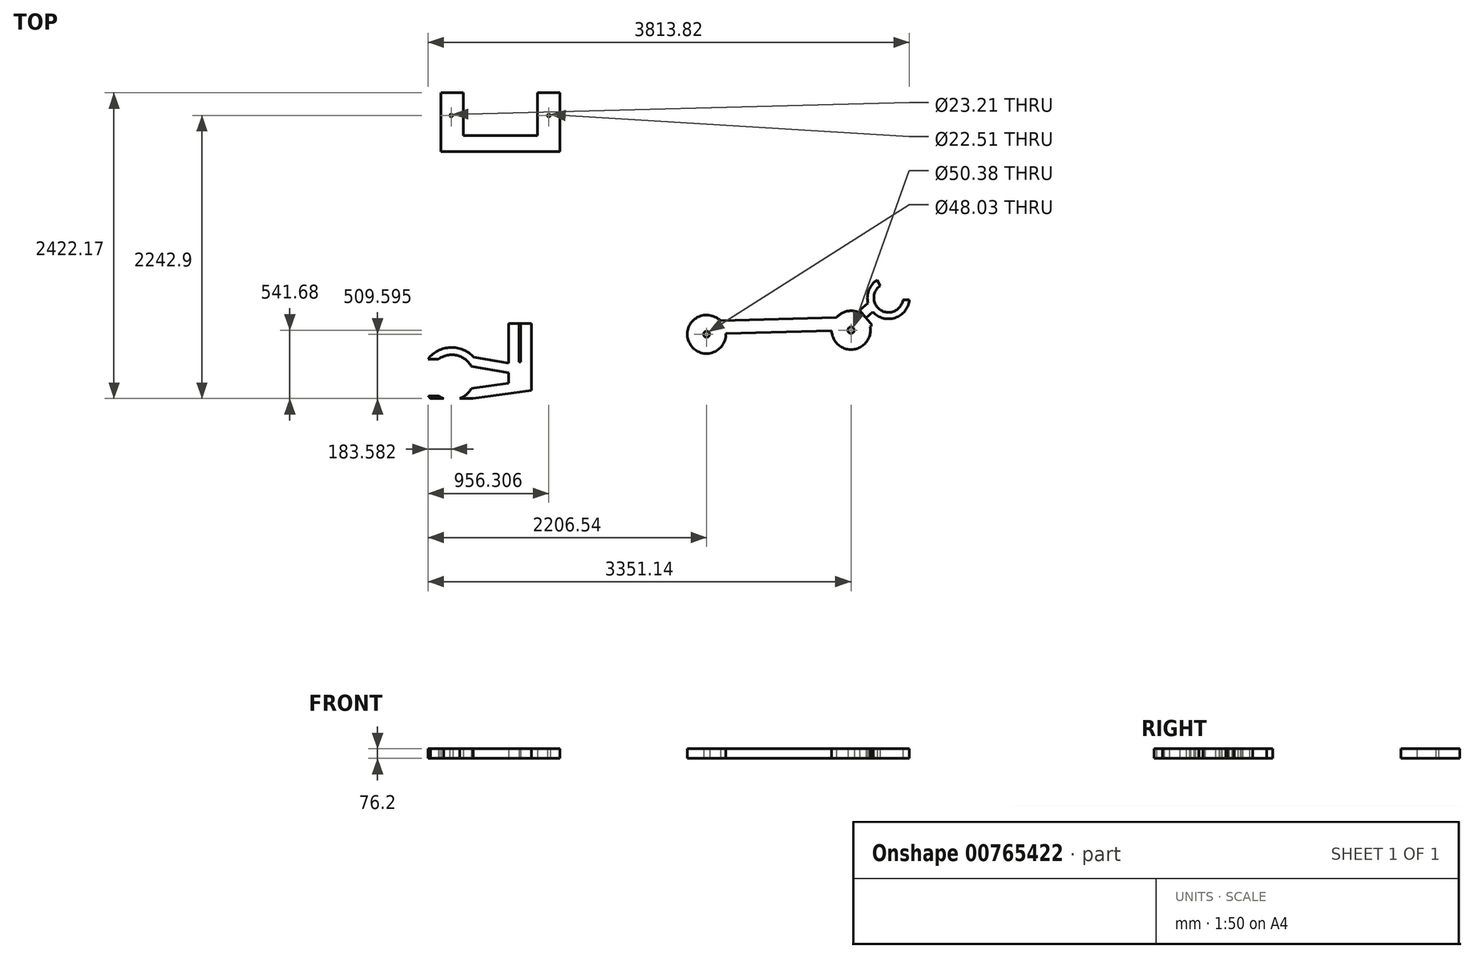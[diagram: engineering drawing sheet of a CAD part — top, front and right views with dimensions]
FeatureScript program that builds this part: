
annotation { "Feature Type Name" : "Feature", "Feature Type Description" : "" }
export const myFeature = defineFeature(function(context is Context, id is Id, definition is map)
    precondition{}
    {
        {
            var Q0;
            Q0=qCreatedBy(makeId("Top.planeOp"),FACE);
            var sketch = newSketch(context, id + "F0", { "sketchPlane" : qUnion([Q0])});
            skCircle(sketch, "E0", {"center": v(-167.25, 5.31) * mm, "radius": 152.85 * mm});
            skLineSegment(sketch, "E1", {"start": v(-167.25, 5.31) * mm, "end": v(977.35, 37.4) * mm});
            skCircle(sketch, "E2", {"center": v(977.35, 37.4) * mm, "radius": 153.41 * mm});
            skLineSegment(sketch, "E3", {"start": v(405.05, 21.36) * mm, "end": v(407.92, -80.8) * mm});
            skLineSegment(sketch, "E4", {"start": v(407.92, -80.8) * mm, "end": v(405.05, 21.36) * mm});
            skLineSegment(sketch, "E5", {"start": v(405.05, 21.36) * mm, "end": v(402.17, 124.37) * mm});
            skLineSegment(sketch, "E6", {"start": v(402.17, 124.37) * mm, "end": v(960.37, 140.02) * mm});
            skLineSegment(sketch, "E7", {"start": v(402.17, 124.37) * mm, "end": v(-140.1, 109.17) * mm});
            skLineSegment(sketch, "E8", {"start": v(407.92, -80.8) * mm, "end": v(-155.3, -80.8) * mm});
            skLineSegment(sketch, "E9", {"start": v(407.92, -80.8) * mm, "end": v(986.6, -64.59) * mm});
            skLineSegment(sketch, "E10", {"start": v(986.6, -64.59) * mm, "end": v(960.37, 122.33) * mm});
            skLineSegment(sketch, "E11", {"start": v(-155.3, -80.8) * mm, "end": v(-140.1, 109.17) * mm});
            skLineSegment(sketch, "E12", {"start": v(960.37, 122.33) * mm, "end": v(960.37, 140.02) * mm});
            skLineSegment(sketch, "E13", {"start": v(977.35, 37.4) * mm, "end": v(1190.16, 214.86) * mm});
            skLineSegment(sketch, "E14", {"start": v(1095.18, 135.65) * mm, "end": v(1044.8, 196.07) * mm});
            skLineSegment(sketch, "E15", {"start": v(1044.8, 196.07) * mm, "end": v(1144.24, 76.82) * mm});
            skLineSegment(sketch, "E16", {"start": v(1144.24, 76.82) * mm, "end": v(1240.32, 156.95) * mm});
            skLineSegment(sketch, "E17", {"start": v(1240.32, 156.95) * mm, "end": v(1095.18, 35.9) * mm});
            skLineSegment(sketch, "E18", {"start": v(1095.18, 35.9) * mm, "end": v(998.06, 152.36) * mm});
            skLineSegment(sketch, "E19", {"start": v(1044.8, 196.07) * mm, "end": v(995.52, 154.98) * mm});
            skLineSegment(sketch, "E20", {"start": v(995.52, 154.98) * mm, "end": v(1139.78, 275.28) * mm});
            skCircle(sketch, "E21", {"center": v(1273.88, 293.87) * mm, "radius": 115.64 * mm});
            skCircle(sketch, "E22", {"center": v(1273.88, 293.87) * mm, "radius": 166.9 * mm});
            skLineSegment(sketch, "E23", {"start": v(1185.71, 435.58) * mm, "end": v(1207.84, 388.8) * mm});
            skLineSegment(sketch, "E24", {"start": v(1388.44, 278.11) * mm, "end": v(1440.03, 278.11) * mm});
            skCircle(sketch, "E25", {"center": v(-167.25, 5.31) * mm, "radius": 24.02 * mm});
            skCircle(sketch, "E26", {"center": v(977.35, 37.4) * mm, "radius": 25.2 * mm});
            skSolve(sketch);
        }
        {
            var Q0;
            {var subQ0=sQuery(id+"F0.wireOp",EDGE,"E17");var subQ3=sQuery(id+"F0.wireOp",EDGE,"E15");var subQ5=makeQuery(id+"F0.imprint","INTERSECT",VERTEX,{"derivedFrom":[subQ3,subQ0]});Q0=makeQuery(id+"F0.imprint","IMPRINT",FACE,{"disambiguationData":[TD([[makeQuery(id+"F0.imprint","IMPRINT",EDGE,{"disambiguationData":[TD([[subQ5,-1.0]])],"derivedFrom":subQ0}),-1.0]])]});}
            var Q1;
            {var subQ0=sQuery(id+"F0.wireOp",EDGE,"E20");var subQ3=sQuery(id+"F0.wireOp",EDGE,"E15");var subQ5=makeQuery(id+"F0.imprint","INTERSECT",VERTEX,{"derivedFrom":[subQ3,subQ0]});Q1=makeQuery(id+"F0.imprint","IMPRINT",FACE,{"disambiguationData":[TD([[makeQuery(id+"F0.imprint","IMPRINT",EDGE,{"disambiguationData":[TD([[subQ5,1.0]])],"derivedFrom":subQ0}),-1.0]])]});}
            var Q2;
            {var subQ5=sQuery(id+"F0.wireOp",EDGE,"E5");Q2=makeQuery(id+"F0.imprint","IMPRINT",FACE,{"disambiguationData":[TD([[makeQuery(id+"F0.imprint","IMPRINT",EDGE,{"derivedFrom":subQ5}),1.0]])]});}
            var Q3;
            {var subQ5=sQuery(id+"F0.wireOp",EDGE,"E0");var subQ7=sQuery(id+"F0.wireOp",EDGE,"E7");var subQ8=makeQuery(id+"F0.imprint","INTERSECT",VERTEX,{"derivedFrom":[subQ5,subQ7]});Q3=makeQuery(id+"F0.imprint","IMPRINT",FACE,{"disambiguationData":[TD([[makeQuery(id+"F0.imprint","IMPRINT",EDGE,{"disambiguationData":[TD([[subQ8,-1.0]])],"derivedFrom":subQ5}),1.0]])]});}
            var Q4;
            {var subQ5=sQuery(id+"F0.wireOp",EDGE,"E4");Q4=makeQuery(id+"F0.imprint","IMPRINT",FACE,{"disambiguationData":[TD([[makeQuery(id+"F0.imprint","IMPRINT",EDGE,{"derivedFrom":subQ5}),1.0]])]});}
            var Q5;
            {var subQ0=sQuery(id+"F0.wireOp",EDGE,"E5");Q5=makeQuery(id+"F0.imprint","IMPRINT",FACE,{"disambiguationData":[TD([[makeQuery(id+"F0.imprint","IMPRINT",EDGE,{"derivedFrom":subQ0}),-1.0]])]});}
            var Q6;
            {var subQ0=sQuery(id+"F0.wireOp",EDGE,"E4");Q6=makeQuery(id+"F0.imprint","IMPRINT",FACE,{"disambiguationData":[TD([[makeQuery(id+"F0.imprint","IMPRINT",EDGE,{"derivedFrom":subQ0}),-1.0]])]});}
            var Q7;
            {var subQ0=sQuery(id+"F0.wireOp",EDGE,"E17");var subQ5=sQuery(id+"F0.wireOp",EDGE,"E18");var subQ6=makeQuery(id+"F0.imprint","INTERSECT",VERTEX,{"derivedFrom":[subQ0,subQ5]});Q7=makeQuery(id+"F0.imprint","IMPRINT",FACE,{"disambiguationData":[TD([[makeQuery(id+"F0.imprint","IMPRINT",EDGE,{"disambiguationData":[TD([[subQ6,1.0]])],"derivedFrom":subQ0}),-1.0]])]});}
            var Q8;
            {var subQ3=sQuery(id+"F0.wireOp",EDGE,"E15");var subQ5=sQuery(id+"F0.wireOp",EDGE,"E20");var subQ6=makeQuery(id+"F0.imprint","INTERSECT",VERTEX,{"derivedFrom":[subQ3,subQ5]});Q8=makeQuery(id+"F0.imprint","IMPRINT",FACE,{"disambiguationData":[TD([[makeQuery(id+"F0.imprint","IMPRINT",EDGE,{"disambiguationData":[TD([[subQ6,-1.0]])],"derivedFrom":subQ5}),-1.0]])]});}
            var Q9;
            {var subQ3=sQuery(id+"F0.wireOp",EDGE,"E15");var subQ5=sQuery(id+"F0.wireOp",EDGE,"E17");var subQ7=makeQuery(id+"F0.imprint","INTERSECT",VERTEX,{"derivedFrom":[subQ3,subQ5]});Q9=makeQuery(id+"F0.imprint","IMPRINT",FACE,{"disambiguationData":[TD([[makeQuery(id+"F0.imprint","IMPRINT",EDGE,{"disambiguationData":[TD([[subQ7,1.0]])],"derivedFrom":subQ5}),-1.0]])]});}
            var Q10;
            {var subQ1=sQuery(id+"F0.wireOp",EDGE,"E7");var subQ5=sQuery(id+"F0.wireOp",EDGE,"E0");var subQ6=makeQuery(id+"F0.imprint","INTERSECT",VERTEX,{"derivedFrom":[subQ5,subQ1]});Q10=makeQuery(id+"F0.imprint","IMPRINT",FACE,{"disambiguationData":[TD([[makeQuery(id+"F0.imprint","IMPRINT",EDGE,{"disambiguationData":[TD([[subQ6,1.0]])],"derivedFrom":subQ5}),1.0]])]});}
            var Q11;
            {var subQ1=sQuery(id+"F0.wireOp",EDGE,"E8");var subQ5=sQuery(id+"F0.wireOp",EDGE,"E0");var subQ6=makeQuery(id+"F0.imprint","INTERSECT",VERTEX,{"derivedFrom":[subQ5,subQ1]});Q11=makeQuery(id+"F0.imprint","IMPRINT",FACE,{"disambiguationData":[TD([[makeQuery(id+"F0.imprint","IMPRINT",EDGE,{"disambiguationData":[TD([[subQ6,-1.0]])],"derivedFrom":subQ5}),1.0]])]});}
            var Q12;
            {var subQ0=sQuery(id+"F0.wireOp",EDGE,"E12");Q12=makeQuery(id+"F0.imprint","IMPRINT",FACE,{"disambiguationData":[TD([[makeQuery(id+"F0.imprint","IMPRINT",EDGE,{"derivedFrom":subQ0}),1.0]])]});}
            var Q13;
            {var subQ5=sQuery(id+"F0.wireOp",EDGE,"E2");var subQ7=sQuery(id+"F0.wireOp",EDGE,"E1");var subQ8=makeQuery(id+"F0.imprint","INTERSECT",VERTEX,{"derivedFrom":[subQ7,subQ5]});Q13=makeQuery(id+"F0.imprint","IMPRINT",FACE,{"disambiguationData":[TD([[makeQuery(id+"F0.imprint","IMPRINT",EDGE,{"disambiguationData":[TD([[subQ8,-1.0]])],"derivedFrom":subQ7}),-1.0]])]});}
            var Q14;
            {var subQ8=sQuery(id+"F0.wireOp",EDGE,"E2");var subQ11=sQuery(id+"F0.wireOp",EDGE,"E17");var subQ12=makeQuery(id+"F0.imprint","INTERSECT",VERTEX,{"derivedFrom":[subQ8,subQ11]});Q14=makeQuery(id+"F0.imprint","IMPRINT",FACE,{"disambiguationData":[TD([[makeQuery(id+"F0.imprint","IMPRINT",EDGE,{"disambiguationData":[TD([[subQ12,1.0]])],"derivedFrom":subQ8}),1.0]])]});}
            var Q15;
            {var subQ4=sQuery(id+"F0.wireOp",EDGE,"E23");Q15=makeQuery(id+"F0.imprint","IMPRINT",FACE,{"disambiguationData":[TD([[makeQuery(id+"F0.imprint","IMPRINT",EDGE,{"derivedFrom":subQ4}),-1.0]])]});}
            var Q16;
            {var subQ4=sQuery(id+"F0.wireOp",EDGE,"E24");Q16=makeQuery(id+"F0.imprint","IMPRINT",FACE,{"disambiguationData":[TD([[makeQuery(id+"F0.imprint","IMPRINT",EDGE,{"derivedFrom":subQ4}),-1.0]])]});}
            var Q17;
            {var subQ0=sQuery(id+"F0.wireOp",EDGE,"E12");Q17=makeQuery(id+"F0.imprint","IMPRINT",FACE,{"disambiguationData":[TD([[makeQuery(id+"F0.imprint","IMPRINT",EDGE,{"derivedFrom":subQ0}),-1.0]])]});}
            extrude(context, id + "F1", {"entities" : qUnion([Q0, Q1, Q2, Q3, Q4, Q5, Q6, Q7, Q8, Q9, Q10, Q11, Q12, Q13, Q14, Q15, Q16, Q17]), "depth" : 76.2 * mm, "offsetDistance" : 25.4 * mm});
        }
        {
            var Q0;
            Q0=qCreatedBy(makeId("Top.planeOp"),FACE);
            var sketch = newSketch(context, id + "F2", { "sketchPlane" : qUnion([Q0])});
            skLineSegment(sketch, "E27.bottom", {"start": v(-1735.68, 90.3) * mm, "end": v(-1556.35, 90.3) * mm});
            skLineSegment(sketch, "E27.top", {"start": v(-1735.68, -438.7) * mm, "end": v(-1556.35, -438.7) * mm});
            skLineSegment(sketch, "E27.left", {"start": v(-1735.68, 90.3) * mm, "end": v(-1735.68, -438.7) * mm});
            skLineSegment(sketch, "E27.right", {"start": v(-1556.35, 90.3) * mm, "end": v(-1556.35, -438.7) * mm});
            skLineSegment(sketch, "E28", {"start": v(-1735.68, 90.3) * mm, "end": v(-1646.02, 90.3) * mm});
            skLineSegment(sketch, "E29", {"start": v(-1646.02, 90.3) * mm, "end": v(-1556.35, 90.3) * mm});
            skLineSegment(sketch, "E30", {"start": v(-1652.05, 90.42) * mm, "end": v(-1639.27, 90.3) * mm});
            skLineSegment(sketch, "E31", {"start": v(-1639.27, 90.3) * mm, "end": v(-1642.15, -215.01) * mm});
            skLineSegment(sketch, "E32", {"start": v(-1652.05, 90.42) * mm, "end": v(-1654.93, -214.97) * mm});
            skLineSegment(sketch, "E33", {"start": v(-1654.93, -214.97) * mm, "end": v(-1642.15, -215.01) * mm});
            skLineSegment(sketch, "E34", {"start": v(-1556.35, -438.7) * mm, "end": v(-2019.08, -504.28) * mm});
            skLineSegment(sketch, "E35", {"start": v(-2019.08, -504.28) * mm, "end": v(-2030.43, -424.16) * mm});
            skLineSegment(sketch, "E36", {"start": v(-2030.43, -424.16) * mm, "end": v(-1556.35, -356.98) * mm});
            skLineSegment(sketch, "E37", {"start": v(-1735.68, -382.4) * mm, "end": v(-1735.68, -300.97) * mm});
            skLineSegment(sketch, "E38", {"start": v(-1735.68, -300.97) * mm, "end": v(-2030.43, -249.14) * mm});
            skLineSegment(sketch, "E39", {"start": v(-2030.43, -249.14) * mm, "end": v(-2030.43, -172.8) * mm});
            skLineSegment(sketch, "E40", {"start": v(-2030.43, -172.8) * mm, "end": v(-1735.68, -224.63) * mm});
            skArc(sketch, "E41", {"start": v(-2030.43, -249.14) * mm, "mid": v(-2366.01, -336.65) * mm, "end": v(-2030.43, -424.16) * mm});
            skCircle(sketch, "E42", {"center": v(-2186.81, -336.65) * mm, "radius": 237.14 * mm});
            skLineSegment(sketch, "E43", {"start": v(-2015.39, -172.8) * mm, "end": v(-2373.79, -172.8) * mm});
            skLineSegment(sketch, "E44", {"start": v(-2019.08, -504.28) * mm, "end": v(-2372.28, -504.28) * mm});
            skLineSegment(sketch, "E45", {"start": v(-2373.79, -190.8) * mm, "end": v(-2300.01, -197.73) * mm});
            skLineSegment(sketch, "E46", {"start": v(-2372.28, -484.41) * mm, "end": v(-2288.2, -484.41) * mm});
            skLineSegment(sketch, "E47", {"start": v(-2373.79, -190.8) * mm, "end": v(-2290.93, -190.8) * mm});
            skSolve(sketch);
        }
        {
            var Q0;
            {var subQ5=sQuery(id+"F2.wireOp",EDGE,"E30");Q0=makeQuery(id+"F2.imprint","IMPRINT",FACE,{"disambiguationData":[TD([[makeQuery(id+"F2.imprint","IMPRINT",EDGE,{"derivedFrom":subQ5}),-1.0]])]});}
            var Q1;
            {var subQ0=sQuery(id+"F2.wireOp",EDGE,"E27.top");Q1=makeQuery(id+"F2.imprint","IMPRINT",FACE,{"disambiguationData":[TD([[makeQuery(id+"F2.imprint","IMPRINT",EDGE,{"derivedFrom":subQ0}),1.0]])]});}
            var Q2;
            {var subQ0=sQuery(id+"F2.wireOp",EDGE,"E43");var subQ3=sQuery(id+"F2.wireOp",EDGE,"E42");var subQ5=makeQuery(id+"F2.imprint","INTERSECT",VERTEX,{"disambiguationData":[OD(0.0)],"derivedFrom":[subQ3,subQ0]});Q2=makeQuery(id+"F2.imprint","IMPRINT",FACE,{"disambiguationData":[TD([[makeQuery(id+"F2.imprint","IMPRINT",EDGE,{"disambiguationData":[TD([[subQ5,1.0]])],"derivedFrom":subQ3}),1.0]])]});}
            var Q3;
            {var subQ5=sQuery(id+"F2.wireOp",EDGE,"E27.top");Q3=makeQuery(id+"F2.imprint","IMPRINT",FACE,{"disambiguationData":[TD([[makeQuery(id+"F2.imprint","IMPRINT",EDGE,{"derivedFrom":subQ5}),-1.0]])]});}
            var Q4;
            {var subQ1=sQuery(id+"F2.wireOp",EDGE,"E27.left");var subQ3=sQuery(id+"F2.wireOp",EDGE,"E40");var subQ4=makeQuery(id+"F2.imprint","INTERSECT",VERTEX,{"derivedFrom":[subQ1,subQ3]});Q4=makeQuery(id+"F2.imprint","IMPRINT",FACE,{"disambiguationData":[TD([[makeQuery(id+"F2.imprint","IMPRINT",EDGE,{"disambiguationData":[TD([[subQ4,1.0]])],"derivedFrom":subQ3}),-1.0]])]});}
            var Q5;
            {var subQ0=sQuery(id+"F2.wireOp",EDGE,"E35");Q5=makeQuery(id+"F2.imprint","IMPRINT",FACE,{"disambiguationData":[TD([[makeQuery(id+"F2.imprint","IMPRINT",EDGE,{"derivedFrom":subQ0}),-1.0]])]});}
            var Q6;
            {var subQ0=sQuery(id+"F2.wireOp",EDGE,"E35");Q6=makeQuery(id+"F2.imprint","IMPRINT",FACE,{"disambiguationData":[TD([[makeQuery(id+"F2.imprint","IMPRINT",EDGE,{"derivedFrom":subQ0}),1.0]])]});}
            var Q7;
            {var subQ0=sQuery(id+"F2.wireOp",EDGE,"E47");Q7=makeQuery(id+"F2.imprint","IMPRINT",FACE,{"disambiguationData":[TD([[makeQuery(id+"F2.imprint","IMPRINT",EDGE,{"derivedFrom":subQ0}),1.0]])]});}
            var Q8;
            {var subQ0=sQuery(id+"F2.wireOp",EDGE,"E46");Q8=makeQuery(id+"F2.imprint","IMPRINT",FACE,{"disambiguationData":[TD([[makeQuery(id+"F2.imprint","IMPRINT",EDGE,{"derivedFrom":subQ0}),-1.0]])]});}
            var Q9;
            {var subQ0=sQuery(id+"F2.wireOp",EDGE,"E44");var subQ1=sQuery(id+"F2.wireOp",EDGE,"E41");var subQ2=makeQuery(id+"F2.imprint","INTERSECT",VERTEX,{"disambiguationData":[OD(0.0)],"derivedFrom":[subQ1,subQ0]});Q9=makeQuery(id+"F2.imprint","IMPRINT",FACE,{"disambiguationData":[TD([[makeQuery(id+"F2.imprint","IMPRINT",EDGE,{"disambiguationData":[TD([[subQ2,-1.0]])],"derivedFrom":subQ1}),-1.0]])]});}
            var Q10;
            {var subQ13=sQuery(id+"F2.wireOp",EDGE,"E31");Q10=makeQuery(id+"F2.imprint","IMPRINT",FACE,{"disambiguationData":[TD([[makeQuery(id+"F2.imprint","IMPRINT",EDGE,{"derivedFrom":subQ13}),1.0]])]});}
            var Q11;
            {var subQ0=sQuery(id+"F2.wireOp",EDGE,"E39");Q11=makeQuery(id+"F2.imprint","IMPRINT",FACE,{"disambiguationData":[TD([[makeQuery(id+"F2.imprint","IMPRINT",EDGE,{"derivedFrom":subQ0}),-1.0]])]});}
            var Q12;
            {var subQ0=sQuery(id+"F2.wireOp",EDGE,"E43");var subQ2=sQuery(id+"F2.wireOp",EDGE,"E41");var subQ3=makeQuery(id+"F2.imprint","INTERSECT",VERTEX,{"disambiguationData":[OD(0.0)],"derivedFrom":[subQ2,subQ0]});Q12=makeQuery(id+"F2.imprint","IMPRINT",FACE,{"disambiguationData":[TD([[makeQuery(id+"F2.imprint","IMPRINT",EDGE,{"disambiguationData":[TD([[subQ3,-1.0]])],"derivedFrom":subQ2}),-1.0]])]});}
            var Q13;
            {var subQ0=sQuery(id+"F2.wireOp",EDGE,"E39");Q13=makeQuery(id+"F2.imprint","IMPRINT",FACE,{"disambiguationData":[TD([[makeQuery(id+"F2.imprint","IMPRINT",EDGE,{"derivedFrom":subQ0}),1.0]])]});}
            extrude(context, id + "F3", {"entities" : qUnion([Q0, Q1, Q2, Q3, Q4, Q5, Q6, Q7, Q8, Q9, Q10, Q11, Q12, Q13]), "depth" : 76.2 * mm, "offsetDistance" : 25.4 * mm});
        }
        {
            var Q0;
            Q0=qCreatedBy(makeId("Top.planeOp"),FACE);
            var sketch = newSketch(context, id + "F4", { "sketchPlane" : qUnion([Q0])});
            skLineSegment(sketch, "E48.bottom", {"start": v(-2095, 1917.9) * mm, "end": v(-1506.03, 1917.9) * mm});
            skLineSegment(sketch, "E48.top", {"start": v(-2095, 1579.82) * mm, "end": v(-1506.03, 1579.82) * mm});
            skLineSegment(sketch, "E48.left", {"start": v(-2095, 1917.9) * mm, "end": v(-2095, 1579.82) * mm});
            skLineSegment(sketch, "E48.right", {"start": v(-1506.03, 1917.9) * mm, "end": v(-1506.03, 1579.82) * mm});
            skLineSegment(sketch, "E49.bottom", {"start": v(-2095, 1917.9) * mm, "end": v(-2272.26, 1917.9) * mm});
            skLineSegment(sketch, "E49.top", {"start": v(-2095, 1579.82) * mm, "end": v(-2272.26, 1579.82) * mm});
            skLineSegment(sketch, "E49.right", {"start": v(-2272.26, 1917.9) * mm, "end": v(-2272.26, 1579.82) * mm});
            skLineSegment(sketch, "E50.bottom", {"start": v(-1506.03, 1917.9) * mm, "end": v(-1329.17, 1917.9) * mm});
            skLineSegment(sketch, "E50.top", {"start": v(-1506.03, 1917.9) * mm, "end": v(-1329.17, 1917.9) * mm});
            skLineSegment(sketch, "E50.left", {"start": v(-1506.03, 1917.9) * mm, "end": v(-1506.03, 1917.9) * mm});
            skLineSegment(sketch, "E50.right", {"start": v(-1329.17, 1917.9) * mm, "end": v(-1329.17, 1917.9) * mm});
            skLineSegment(sketch, "E51.bottom", {"start": v(-1329.17, 1917.9) * mm, "end": v(-1506.03, 1917.9) * mm});
            skLineSegment(sketch, "E51.top", {"start": v(-1329.17, 1579.82) * mm, "end": v(-1506.03, 1579.82) * mm});
            skLineSegment(sketch, "E51.left", {"start": v(-1329.17, 1917.9) * mm, "end": v(-1329.17, 1579.82) * mm});
            skLineSegment(sketch, "E52.bottom", {"start": v(-2272.26, 1579.82) * mm, "end": v(-2272.26, 1579.82) * mm});
            skLineSegment(sketch, "E52.top", {"start": v(-2272.26, 1452.36) * mm, "end": v(-2272.26, 1452.36) * mm});
            skLineSegment(sketch, "E52.left", {"start": v(-2272.26, 1579.82) * mm, "end": v(-2272.26, 1452.36) * mm});
            skLineSegment(sketch, "E52.right", {"start": v(-2272.26, 1579.82) * mm, "end": v(-2272.26, 1452.36) * mm});
            skLineSegment(sketch, "E53.bottom", {"start": v(-2272.26, 1579.82) * mm, "end": v(-1329.17, 1579.82) * mm});
            skLineSegment(sketch, "E53.top", {"start": v(-2272.26, 1452.36) * mm, "end": v(-1329.17, 1452.36) * mm});
            skLineSegment(sketch, "E53.right", {"start": v(-1329.17, 1579.82) * mm, "end": v(-1329.17, 1452.36) * mm});
            skCircle(sketch, "E54", {"center": v(-2190.2, 1738.62) * mm, "radius": 11.6 * mm});
            skCircle(sketch, "E55", {"center": v(-1417.48, 1738.62) * mm, "radius": 11.26 * mm});
            skSolve(sketch);
        }
        {
            var Q0;
            Q0=makeQuery(id+"F4.imprint","IMPRINT",FACE,{"disambiguationData":[TD([[makeQuery(id+"F4.imprint","IMPRINT",EDGE,{"derivedFrom":sQuery(id+"F4.wireOp",EDGE,"E48.left")}),-1.0]])]});
            var Q1;
            Q1=makeQuery(id+"F4.imprint","IMPRINT",FACE,{"disambiguationData":[TD([[makeQuery(id+"F4.imprint","IMPRINT",EDGE,{"derivedFrom":sQuery(id+"F4.wireOp",EDGE,"E48.top")}),-1.0]])]});
            var Q2;
            Q2=makeQuery(id+"F4.imprint","IMPRINT",FACE,{"disambiguationData":[TD([[makeQuery(id+"F4.imprint","IMPRINT",EDGE,{"derivedFrom":sQuery(id+"F4.wireOp",EDGE,"E48.right")}),1.0]])]});
            extrude(context, id + "F5", {"entities" : qUnion([Q0, Q1, Q2]), "depth" : 76.2 * mm, "offsetDistance" : 25.4 * mm});
        }
    });
